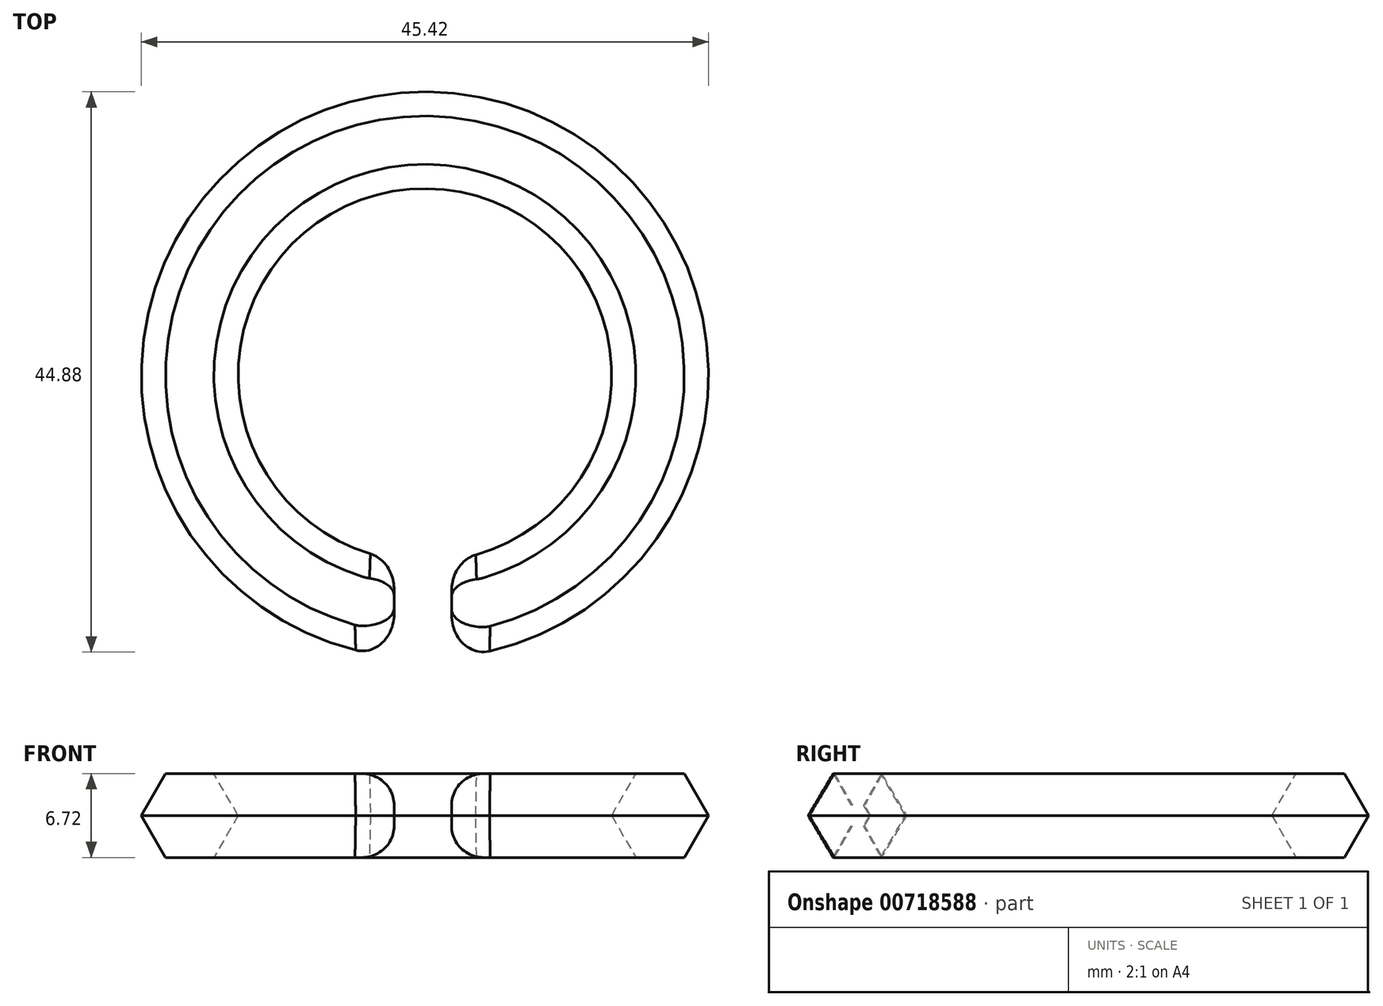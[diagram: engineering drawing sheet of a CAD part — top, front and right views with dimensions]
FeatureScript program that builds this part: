
annotation { "Feature Type Name" : "Feature", "Feature Type Description" : "" }
export const myFeature = defineFeature(function(context is Context, id is Id, definition is map)
    precondition{}
    {
        {
            var Q0;
            Q0=qCreatedBy(makeId("Front.planeOp"),FACE);
            var sketch = newSketch(context, id + "F0", { "sketchPlane" : qUnion([Q0])});
            skLineSegment(sketch, "E0", {"start": v(0, 39.27) * mm, "end": v(0, -21.75) * mm});
            skCircle(sketch, "E1.cCircle", {"center": v(-18.83, 0) * mm, "radius": 3.36 * mm, "construction": true});
            skLineSegment(sketch, "E1.0", {"start": v(-16.9, -3.36) * mm, "end": v(-20.77, -3.36) * mm});
            skLineSegment(sketch, "E1.1", {"start": v(-20.77, -3.36) * mm, "end": v(-22.71, 0) * mm});
            skLineSegment(sketch, "E1.2", {"start": v(-22.71, 0) * mm, "end": v(-20.77, 3.36) * mm});
            skLineSegment(sketch, "E1.3", {"start": v(-20.77, 3.36) * mm, "end": v(-16.9, 3.36) * mm});
            skLineSegment(sketch, "E1.4", {"start": v(-16.9, 3.36) * mm, "end": v(-14.96, 0) * mm});
            skLineSegment(sketch, "E1.5", {"start": v(-14.96, 0) * mm, "end": v(-16.9, -3.36) * mm});
            skPoint(sketch, "E1.0.midPoint", {"position": v(-18.83, -3.36) * mm});
            skSolve(sketch);
        }
        {
            var Q0;
            Q0 = qSketchRegion(id + "F0", true);
            var Q1;
            Q1=sQuery(id+"F0.wireOp",EDGE,"E0");
            revolve(context, id + "F1", {"surfaceOperationType" : NewSurfaceOperationType.NEW, "entities" : qUnion([Q0]), "axis" : qUnion([Q1]), "revolveType" : RevolveType.FULL});
        }
        {
            var Q0;
            Q0=qCreatedBy(makeId("Top.planeOp"),FACE);
            var sketch = newSketch(context, id + "F2", { "sketchPlane" : qUnion([Q0])});
            skLineSegment(sketch, "E2.bottom", {"start": v(-2.47, -24.57) * mm, "end": v(2.14, -24.57) * mm});
            skLineSegment(sketch, "E2.top", {"start": v(-2.47, -11.32) * mm, "end": v(2.14, -11.32) * mm});
            skLineSegment(sketch, "E2.left", {"start": v(-2.47, -24.57) * mm, "end": v(-2.47, -11.32) * mm});
            skLineSegment(sketch, "E2.right", {"start": v(2.14, -24.57) * mm, "end": v(2.14, -11.32) * mm});
            skSolve(sketch);
        }
        {
            var Q0;
            Q0 = qSketchRegion(id + "F2", true);
            extrude(context, id + "F3", {"entities" : qUnion([Q0]), "operationType" : NewBodyOperationType.REMOVE, "endBound" : BoundingType.SYMMETRIC, "oppositeDirection" : true, "depth" : 25.4 * mm, "offsetDistance" : 25.4 * mm});
        }
        {
            var Q0;
            Q0=makeQuery(id+"F3.boolean.opBoolean","COPY",FACE,{"derivedFrom":makeQuery(id+"F3.opExtrude","SWEPT_FACE",FACE,{"disambiguationData":[OSD([sQuery(id+"F2.wireOp",EDGE,"E2.right")])]})});
            var Q1;
            Q1=makeQuery(id+"F3.boolean.opBoolean","COPY",FACE,{"derivedFrom":makeQuery(id+"F3.opExtrude","SWEPT_FACE",FACE,{"disambiguationData":[OSD([sQuery(id+"F2.wireOp",EDGE,"E2.left")])]})});
            fillet(context, id + "F4", {"entities" : qUnion([Q0, Q1]), "radius" : 2.54 * mm, "tangentPropagation" : true, "allowEdgeOverflow" : false});
        }
    });
